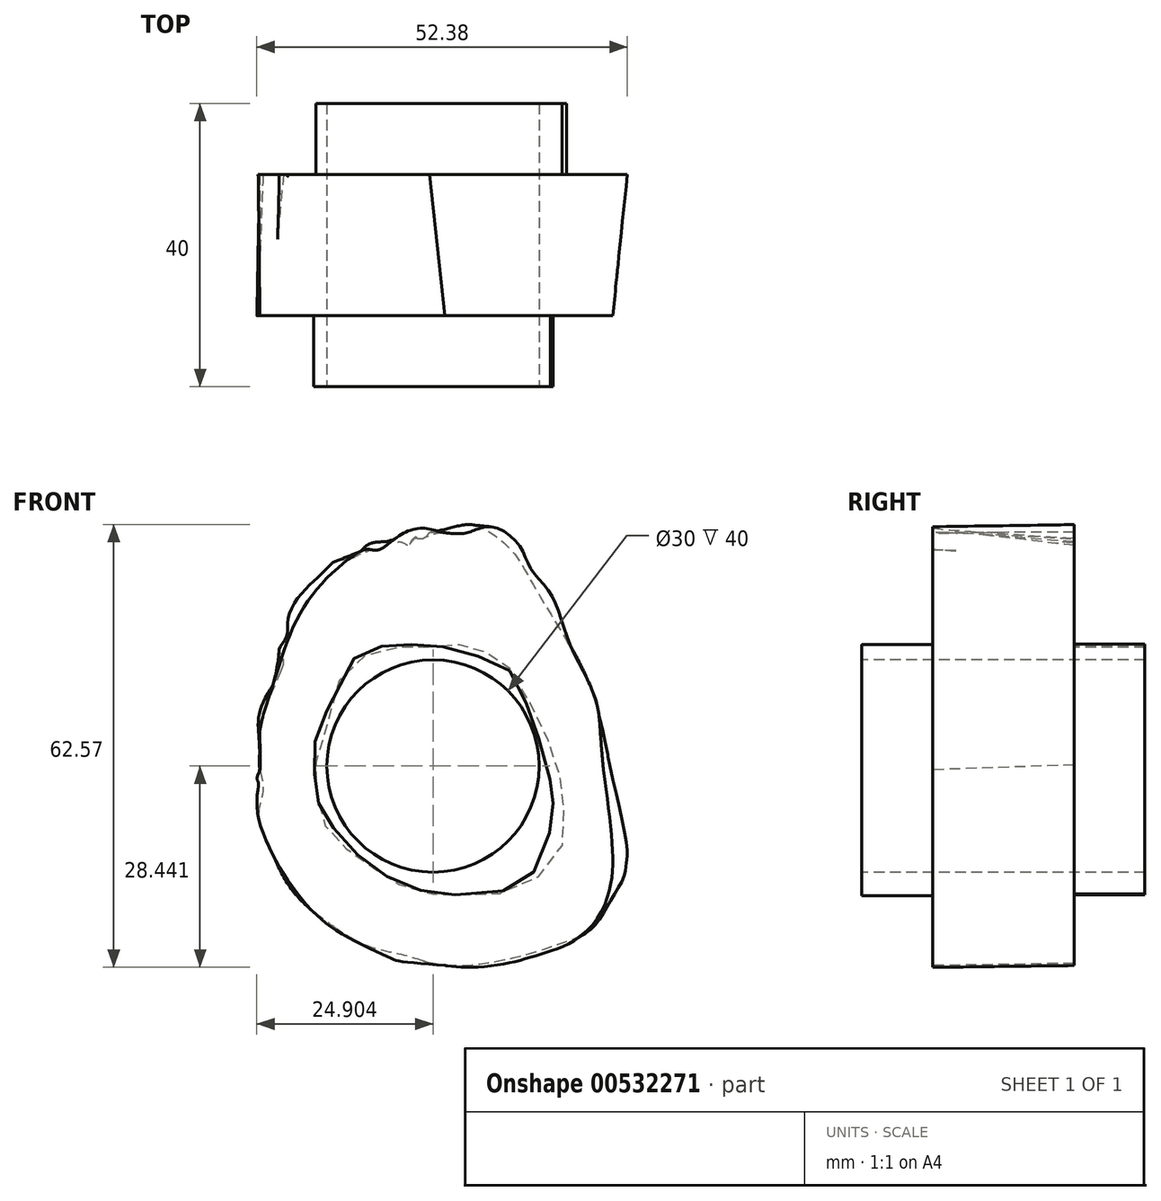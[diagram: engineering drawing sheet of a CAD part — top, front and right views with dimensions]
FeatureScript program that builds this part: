
annotation { "Feature Type Name" : "Feature", "Feature Type Description" : "" }
export const myFeature = defineFeature(function(context is Context, id is Id, definition is map)
    precondition{}
    {
        {
            var Q0;
            Q0=qCreatedBy(makeId("Front.planeOp"),FACE);
            cPlane(context, id + "F0", {"entities" : qUnion([Q0]), "cplaneType" : CPlaneType.OFFSET, "offset" : 20 * mm, "width" : 152.4 * mm, "height" : 152.4 * mm});
        }
        {
            var Q0;
            Q0=qCreatedBy(makeId("Front.planeOp"),FACE);
            var sketch = newSketch(context, id + "F1", { "sketchPlane" : qUnion([Q0])});
            skLineSegment(sketch, "E0", {"start": v(-29.89, -23.03) * mm, "end": v(-29.89, -104.14) * mm, "construction": true});
            skLineSegment(sketch, "E1", {"start": v(-63.04, -65.35) * mm, "end": v(10.67, -65.35) * mm, "construction": true});
            skFitSpline(sketch, "E2", {"points": [v(-29.89, -32.46) * mm, v(-27.6, -32.02) * mm, v(-24.93, -31.42) * mm, v(-22.41, -31.87) * mm, v(-18.26, -35.13) * mm, v(-16.04, -38.54) * mm, v(-11.88, -45.51) * mm, v(-7.88, -52.63) * mm, v(-5.5, -60.2) * mm, v(-4.47, -65.35) * mm], "startDerivative": vector(29.03, 4.92) * mm, "endDerivative": vector(7.76, -42.35) * mm});
            skFitSpline(sketch, "E3", {"points": [v(-29.89, -93.4) * mm, v(-25.82, -93.7) * mm, v(-17.67, -92.52) * mm, v(-10.55, -90.3) * mm, v(-7, -88.51) * mm, v(-4.47, -84.8) * mm, v(-2.4, -80.95) * mm, v(-2.1, -79.17) * mm, v(-1.95, -77.98) * mm, v(-4.47, -65.35) * mm], "startDerivative": vector(36.24, -4.87) * mm, "endDerivative": vector(-20.64, 89.19) * mm});
            skFitSpline(sketch, "E4", {"points": [v(-29.89, -93.4) * mm, v(-33.68, -92.22) * mm, v(-38.87, -90.88) * mm, v(-44.5, -87.47) * mm, v(-49.7, -82.58) * mm, v(-52.66, -76.5) * mm, v(-53.85, -73.54) * mm, v(-53.85, -70.87) * mm, v(-53.4, -68.8) * mm, v(-54, -65.35) * mm], "startDerivative": vector(-34.33, 12.13) * mm, "endDerivative": vector(-9.71, 37.49) * mm});
            skFitSpline(sketch, "E5", {"points": [v(-54, -65.35) * mm, v(-54, -61.97) * mm, v(-53.68, -57.07) * mm, v(-50.53, -50.7) * mm, v(-51.16, -49.09) * mm, v(-50.16, -47.34) * mm, v(-49.91, -44.6) * mm, v(-47.54, -40.6) * mm, v(-44.67, -37.87) * mm, v(-43.05, -36.5) * mm, v(-40.56, -36) * mm, v(-38.44, -34.13) * mm, v(-34.82, -33.88) * mm, v(-33.83, -33.88) * mm, v(-32.83, -34.25) * mm, v(-32.2, -33.38) * mm, v(-30.96, -33.38) * mm, v(-29.89, -32.46) * mm], "startDerivative": vector(1.93, 48.6) * mm, "endDerivative": vector(21.7, 29.33) * mm});
            skSolve(sketch);
        }
        {
            var Q0;
            Q0=qCreatedBy(id+"F0.planeOp",FACE);
            var sketch = newSketch(context, id + "F2", { "sketchPlane" : qUnion([Q0])});
            skLineSegment(sketch, "E6", {"start": v(-27.73, -25.14) * mm, "end": v(-27.73, -105.44) * mm, "construction": true});
            skLineSegment(sketch, "E7", {"start": v(-57.15, -66.04) * mm, "end": v(15.66, -66.04) * mm, "construction": true});
            skFitSpline(sketch, "E8", {"points": [v(-27.73, -32.54) * mm, v(-24.64, -32.54) * mm, v(-21.29, -31.7) * mm, v(-17.3, -34.22) * mm, v(-15.63, -37.57) * mm, v(-12.7, -41.35) * mm, v(-10.17, -48.06) * mm, v(-6.6, -55.6) * mm, v(-5.77, -60.85) * mm, v(-5.35, -66.04) * mm], "startDerivative": vector(35.43, -4.21) * mm, "endDerivative": vector(4.01, -46) * mm});
            skFitSpline(sketch, "E9", {"points": [v(-27.73, -93.7) * mm, v(-24.63, -93.96) * mm, v(-19.17, -93.43) * mm, v(-15.11, -92.37) * mm, v(-10.62, -90.79) * mm, v(-6.38, -87.35) * mm, v(-4.44, -82.85) * mm, v(-4, -79.06) * mm, v(-4.36, -73.77) * mm, v(-5.35, -66.04) * mm], "startDerivative": vector(31.8, -4.38) * mm, "endDerivative": vector(-7.84, 57.27) * mm});
            skFitSpline(sketch, "E10", {"points": [v(-53.87, -66.04) * mm, v(-54.31, -67.39) * mm, v(-54.14, -67.74) * mm, v(-54.31, -71.18) * mm, v(-51.32, -79.47) * mm, v(-46.64, -85.82) * mm, v(-41.8, -89.52) * mm, v(-35.36, -92.7) * mm, v(-34.39, -93.05) * mm, v(-27.73, -93.7) * mm], "startDerivative": vector(-11.19, -25) * mm, "endDerivative": vector(59.28, -4.74) * mm});
            skFitSpline(sketch, "E11", {"points": [v(-53.87, -66.04) * mm, v(-53.87, -63.72) * mm, v(-53.87, -62.56) * mm, v(-53.87, -60.36) * mm, v(-52.03, -53.96) * mm, v(-49.2, -45.9) * mm, v(-45.32, -39.92) * mm, v(-40.6, -35.72) * mm, v(-38.6, -34.88) * mm, v(-37.24, -34.99) * mm, v(-34.83, -33.41) * mm, v(-32.53, -32.16) * mm, v(-30.32, -31.95) * mm, v(-28.65, -32.37) * mm, v(-27.73, -32.54) * mm], "startDerivative": vector(-0.22, 41.14) * mm, "endDerivative": vector(21.77, -3.22) * mm});
            skSolve(sketch);
        }
        {
            var Q0;
            Q0 = qSketchRegion(id + "F1", true);
            var Q1;
            Q1 = qSketchRegion(id + "F2", true);
            loft(context, id + "F3", {"sheetProfilesArray" : [{ "sheetProfileEntities" : qUnion([Q0]) }, { "sheetProfileEntities" : qUnion([Q1]) }]});
        }
        {
            var Q0;
            Q0=qCreatedBy(makeId("Front.planeOp"),FACE);
            var sketch = newSketch(context, id + "F4", { "sketchPlane" : qUnion([Q0])});
            skFitSpline(sketch, "E12", {"points": [v(-29.98, -48.72) * mm, v(-32.36, -48.49) * mm, v(-33.58, -48.72) * mm, v(-36.34, -48.72) * mm, v(-38.8, -49.8) * mm, v(-41.17, -51.32) * mm, v(-42.85, -53.85) * mm, v(-44, -58.67) * mm, v(-45.15, -61.2) * mm, v(-46, -65.03) * mm, v(-45.91, -66.26) * mm, v(-45.91, -69.1) * mm, v(-45.76, -71.54) * mm, v(-44.77, -73.76) * mm, v(-43.54, -75.37) * mm, v(-42, -76.83) * mm, v(-40.48, -78.28) * mm, v(-38.49, -79.43) * mm, v(-36.72, -80.88) * mm, v(-34.89, -81.96) * mm, v(-32.51, -82.88) * mm, v(-29.98, -83.57) * mm, v(-27.84, -83.57) * mm, v(-24.47, -83.72) * mm, v(-22.1, -83.57) * mm, v(-20.72, -83.57) * mm, v(-17.35, -82.8) * mm, v(-13.9, -80.65) * mm, v(-11.83, -78.28) * mm, v(-10.68, -74.91) * mm, v(-10.68, -72.61) * mm, v(-11.22, -70.85) * mm, v(-11.22, -68.25) * mm, v(-12.14, -65.03) * mm, v(-13.14, -61.9) * mm, v(-14.36, -59.06) * mm, v(-16.5, -55.15) * mm, v(-18.04, -52.4) * mm, v(-19.57, -50.7) * mm, v(-20.8, -49.64) * mm, v(-23.17, -49.18) * mm, v(-24.24, -48.34) * mm, v(-26.08, -48.49) * mm, v(-28.38, -48.72) * mm, v(-29.98, -48.72) * mm]});
            skSolve(sketch);
        }
        {
            var Q0;
            Q0 = qSketchRegion(id + "F4", true);
            extrude(context, id + "F5", {"entities" : qUnion([Q0]), "operationType" : NewBodyOperationType.ADD, "oppositeDirection" : true, "depth" : 10 * mm, "offsetDistance" : 25 * mm});
        }
        {
            var Q0;
            Q0=qCreatedBy(id+"F0.planeOp",FACE);
            var sketch = newSketch(context, id + "F6", { "sketchPlane" : qUnion([Q0])});
            skFitSpline(sketch, "E13", {"points": [v(-28.03, -48.64) * mm, v(-24.8, -49.18) * mm, v(-21.73, -50.62) * mm, v(-19.12, -51.7) * mm, v(-17.41, -53.5) * mm, v(-16.06, -57.1) * mm, v(-14.9, -60.24) * mm, v(-13.73, -64.3) * mm, v(-12.83, -68.07) * mm, v(-12.83, -69.7) * mm, v(-12.47, -70.5) * mm, v(-12.74, -72.03) * mm, v(-12.92, -74.28) * mm, v(-14.08, -79.14) * mm, v(-16.06, -81.2) * mm, v(-18.76, -82.92) * mm, v(-24.7, -83.82) * mm, v(-28.3, -83.46) * mm, v(-31.18, -83.1) * mm, v(-33.6, -82.1) * mm, v(-37.2, -80.4) * mm, v(-39.55, -78.5) * mm, v(-41.98, -76.17) * mm, v(-43.78, -73.92) * mm, v(-44.77, -72.48) * mm, v(-45.76, -70.32) * mm, v(-46.12, -68.43) * mm, v(-46.2, -66.27) * mm, v(-46.3, -63.84) * mm, v(-45.85, -60.87) * mm, v(-44.86, -58.62) * mm, v(-43.78, -56.29) * mm, v(-42.79, -54.49) * mm, v(-42.07, -52.96) * mm, v(-40.9, -50.7) * mm, v(-39.73, -49.54) * mm, v(-37.12, -48.64) * mm, v(-35.4, -48.46) * mm, v(-32.89, -48.37) * mm, v(-30.73, -48.46) * mm, v(-28.03, -48.64) * mm]});
            skSolve(sketch);
        }
        {
            var Q0;
            Q0 = qSketchRegion(id + "F6", true);
            extrude(context, id + "F7", {"entities" : qUnion([Q0]), "operationType" : NewBodyOperationType.ADD, "depth" : 10 * mm, "offsetDistance" : 25 * mm});
        }
        {
            var Q0;
            Q0=makeQuery(id+"F7.opExtrude","CAP_FACE",FACE,{"disambiguationData":[OSD([sQuery(id+"F6.wireOp",EDGE,"E13")])],"isStart":false});
            var sketch = newSketch(context, id + "F8", { "sketchPlane" : qUnion([Q0])});
            skCircle(sketch, "E14", {"center": v(-29.43, -65.52) * mm, "radius": 15 * mm});
            skSolve(sketch);
        }
        {
            var Q0;
            Q0 = qSketchRegion(id + "F8", true);
            extrude(context, id + "F9", {"entities" : qUnion([Q0]), "operationType" : NewBodyOperationType.REMOVE, "endBound" : BoundingType.THROUGH_ALL, "oppositeDirection" : true, "depth" : 25 * mm, "offsetDistance" : 25 * mm});
        }
    });
